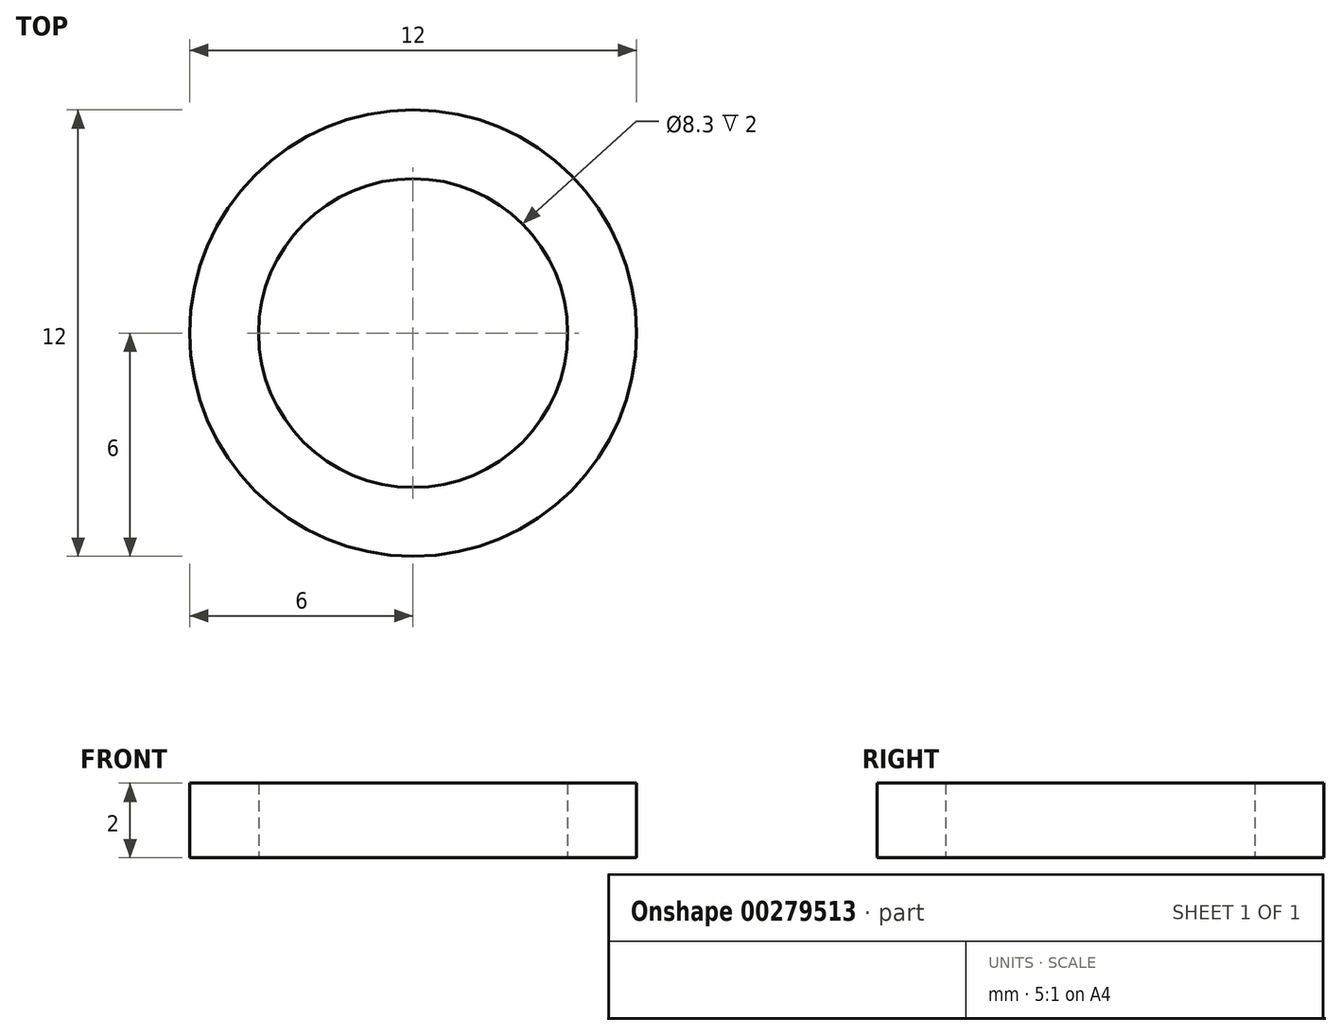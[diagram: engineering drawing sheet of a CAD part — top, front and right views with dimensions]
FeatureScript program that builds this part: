
annotation { "Feature Type Name" : "Feature", "Feature Type Description" : "" }
export const myFeature = defineFeature(function(context is Context, id is Id, definition is map)
    precondition{}
    {
        {
            var Q0;
            Q0=qCreatedBy(makeId("Top.planeOp"),FACE);
            var sketch = newSketch(context, id + "F0", { "sketchPlane" : qUnion([Q0])});
            skCircle(sketch, "E0", {"center": v(0, 0) * mm, "radius": 6 * mm});
            skCircle(sketch, "E1", {"center": v(0, 0) * mm, "radius": 4.15 * mm});
            skSolve(sketch);
        }
        {
            var Q0;
            Q0=makeQuery(id+"F0.imprint","IMPRINT",FACE,{"disambiguationData":[TD([[makeQuery(id+"F0.imprint","IMPRINT",EDGE,{"derivedFrom":sQuery(id+"F0.wireOp",EDGE,"E0")}),1.0]])]});
            extrude(context, id + "F1", {"entities" : qUnion([Q0]), "depth" : 2 * mm});
        }
    });
